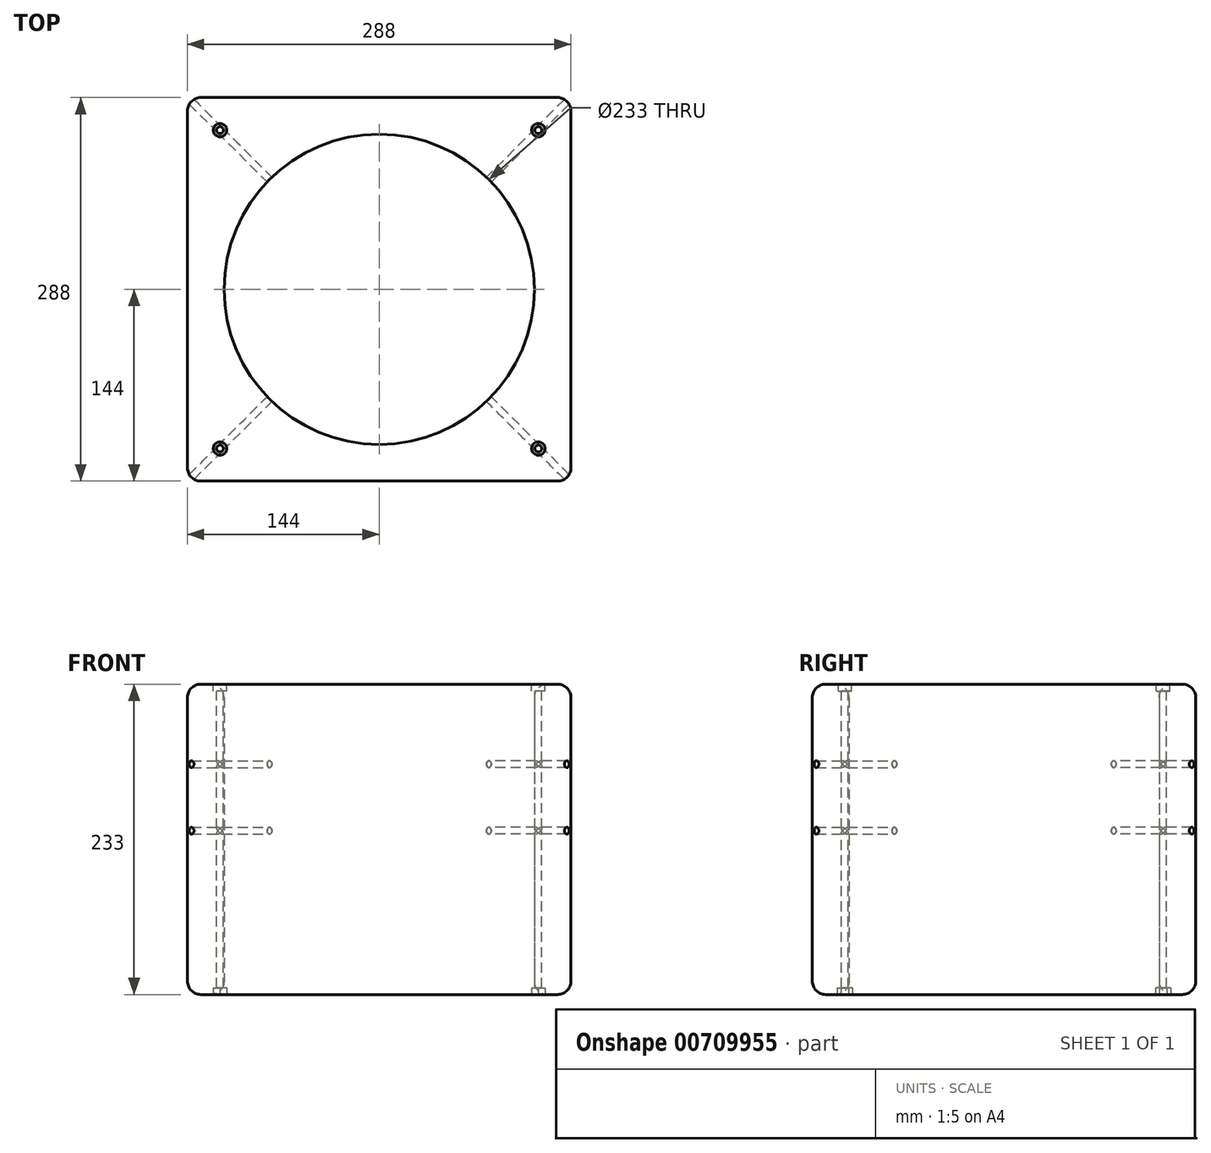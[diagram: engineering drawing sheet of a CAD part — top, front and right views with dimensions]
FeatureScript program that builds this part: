
annotation { "Feature Type Name" : "Feature", "Feature Type Description" : "" }
export const myFeature = defineFeature(function(context is Context, id is Id, definition is map)
    precondition{}
    {
        {
            var Q0;
            Q0=qCreatedBy(makeId("Top.planeOp"),FACE);
            var sketch = newSketch(context, id + "F0", { "sketchPlane" : qUnion([Q0])});
            skCircle(sketch, "E0", {"center": v(0, 0) * mm, "radius": 116.5 * mm});
            skLineSegment(sketch, "E1.bottom", {"start": v(144, 144) * mm, "end": v(-144, 144) * mm});
            skLineSegment(sketch, "E1.top", {"start": v(144, -144) * mm, "end": v(-144, -144) * mm});
            skLineSegment(sketch, "E1.left", {"start": v(144, 144) * mm, "end": v(144, -144) * mm});
            skLineSegment(sketch, "E1.right", {"start": v(-144, 144) * mm, "end": v(-144, -144) * mm});
            skSolve(sketch);
        }
        {
            var Q0;
            Q0=makeQuery(id+"F0.imprint","IMPRINT",FACE,{"disambiguationData":[TD([[makeQuery(id+"F0.imprint","IMPRINT",EDGE,{"derivedFrom":sQuery(id+"F0.wireOp",EDGE,"E0")}),-1.0]])]});
            extrude(context, id + "F1", {"entities" : qUnion([Q0]), "depth" : 233 * mm, "offsetDistance" : 25 * mm});
        }
        {
            var Q0;
            Q0=makeQuery(id+"F1.opExtrude","CAP_FACE",FACE,{"disambiguationData":[OSD([sQuery(id+"F0.wireOp",EDGE,"E0"),sQuery(id+"F0.wireOp",EDGE,"E1.bottom"),sQuery(id+"F0.wireOp",EDGE,"E1.top"),sQuery(id+"F0.wireOp",EDGE,"E1.left"),sQuery(id+"F0.wireOp",EDGE,"E1.right")])],"isStart":false});
            var Q1;
            Q1=makeQuery(id+"F1.opExtrude","CAP_FACE",FACE,{"disambiguationData":[OSD([sQuery(id+"F0.wireOp",EDGE,"E0"),sQuery(id+"F0.wireOp",EDGE,"E1.bottom"),sQuery(id+"F0.wireOp",EDGE,"E1.top"),sQuery(id+"F0.wireOp",EDGE,"E1.left"),sQuery(id+"F0.wireOp",EDGE,"E1.right")])],"isStart":true});
            var Q2;
            {var subQ0=sQuery(id+"F0.wireOp",EDGE,"E1.bottom");Q2=makeQuery(id+"Fkc3ZmtWVtNshut_1.opChamfer","BLEND_EDGE",EDGE,{"blendedFrom":[makeQuery(id+"F1.opExtrude","SWEPT_EDGE",EDGE,{"disambiguationData":[OSD([subQ0,sQuery(id+"F0.wireOp",EDGE,"E1.right")])]}),makeQuery(id+"F1.opExtrude","SWEPT_FACE",FACE,{"disambiguationData":[OSD([subQ0])]})],"blendedInto":[makeQuery(id+"F1.opExtrude","SWEPT_FACE",FACE,{"disambiguationData":[OSD([subQ0])]})]});}
            var Q3;
            Q3=makeQuery(id+"F1.opExtrude","SWEPT_FACE",FACE,{"disambiguationData":[OSD([sQuery(id+"F0.wireOp",EDGE,"E1.right")])]});
            var Q4;
            {var subQ0=sQuery(id+"F0.wireOp",EDGE,"E1.top");Q4=makeQuery(id+"Fkc3ZmtWVtNshut_1.opChamfer","BLEND_EDGE",EDGE,{"blendedFrom":[makeQuery(id+"F1.opExtrude","SWEPT_EDGE",EDGE,{"disambiguationData":[OSD([subQ0,sQuery(id+"F0.wireOp",EDGE,"E1.right")])]}),makeQuery(id+"F1.opExtrude","SWEPT_FACE",FACE,{"disambiguationData":[OSD([subQ0])]})],"blendedInto":[makeQuery(id+"F1.opExtrude","SWEPT_FACE",FACE,{"disambiguationData":[OSD([subQ0])]})]});}
            var Q5;
            {var subQ0=sQuery(id+"F0.wireOp",EDGE,"E1.top");Q5=makeQuery(id+"Fkc3ZmtWVtNshut_1.opChamfer","BLEND_EDGE",EDGE,{"blendedFrom":[makeQuery(id+"F1.opExtrude","SWEPT_EDGE",EDGE,{"disambiguationData":[OSD([subQ0,sQuery(id+"F0.wireOp",EDGE,"E1.left")])]}),makeQuery(id+"F1.opExtrude","SWEPT_FACE",FACE,{"disambiguationData":[OSD([subQ0])]})],"blendedInto":[makeQuery(id+"F1.opExtrude","SWEPT_FACE",FACE,{"disambiguationData":[OSD([subQ0])]})]});}
            var Q6;
            Q6=makeQuery(id+"Fkc3ZmtWVtNshut_1.opChamfer","BLEND_FACE",FACE,{"disambiguationData":[OSD([sQuery(id+"F0.wireOp",EDGE,"E1.top"),sQuery(id+"F0.wireOp",EDGE,"E1.left")])]});
            var Q7;
            Q7=makeQuery(id+"F1.opExtrude","SWEPT_FACE",FACE,{"disambiguationData":[OSD([sQuery(id+"F0.wireOp",EDGE,"E1.left")])]});
            var Q8;
            Q8=makeQuery(id+"Fkc3ZmtWVtNshut_1.opChamfer","BLEND_FACE",FACE,{"disambiguationData":[OSD([sQuery(id+"F0.wireOp",EDGE,"E1.bottom"),sQuery(id+"F0.wireOp",EDGE,"E1.left")])]});
            fillet(context, id + "F2", {"entities" : qUnion([Q0, Q1, Q2, Q3, Q4, Q5, Q6, Q7, Q8]), "radius" : 10 * mm, "tangentPropagation" : true, "allowEdgeOverflow" : false});
        }
        {
            var Q0;
            {var subQ0=sQuery(id+"F0.wireOp",EDGE,"E1.right");var subQ1=sQuery(id+"F0.wireOp",EDGE,"E1.top");Q0=makeQuery(id+"F2.opFillet","BLEND_VERTEX",VERTEX,{"blendedFrom":[makeQuery(id+"F1.opExtrude","CAP_VERTEX",VERTEX,{"disambiguationData":[OSD([subQ1,subQ0])],"isStart":false}),makeQuery(id+"F1.opExtrude","CAP_EDGE",EDGE,{"disambiguationData":[OSD([subQ1])],"isStart":false}),makeQuery(id+"F1.opExtrude","CAP_EDGE",EDGE,{"disambiguationData":[OSD([subQ0])],"isStart":false}),makeQuery(id+"F1.opExtrude","CAP_FACE",FACE,{"disambiguationData":[OSD([sQuery(id+"F0.wireOp",EDGE,"E0"),sQuery(id+"F0.wireOp",EDGE,"E1.bottom"),subQ1,sQuery(id+"F0.wireOp",EDGE,"E1.left"),subQ0])],"isStart":false})],"blendedInto":[makeQuery(id+"F1.opExtrude","CAP_FACE",FACE,{"disambiguationData":[OSD([sQuery(id+"F0.wireOp",EDGE,"E0"),sQuery(id+"F0.wireOp",EDGE,"E1.bottom"),subQ1,sQuery(id+"F0.wireOp",EDGE,"E1.left"),subQ0])],"isStart":false})]});}
            var Q1;
            {var subQ0=sQuery(id+"F0.wireOp",EDGE,"E1.left");var subQ1=sQuery(id+"F0.wireOp",EDGE,"E1.bottom");Q1=makeQuery(id+"F2.opFillet","BLEND_VERTEX",VERTEX,{"blendedFrom":[makeQuery(id+"F1.opExtrude","CAP_VERTEX",VERTEX,{"disambiguationData":[OSD([subQ1,subQ0])],"isStart":false}),makeQuery(id+"F1.opExtrude","CAP_EDGE",EDGE,{"disambiguationData":[OSD([subQ1])],"isStart":false}),makeQuery(id+"F1.opExtrude","CAP_EDGE",EDGE,{"disambiguationData":[OSD([subQ0])],"isStart":false}),makeQuery(id+"F1.opExtrude","CAP_FACE",FACE,{"disambiguationData":[OSD([sQuery(id+"F0.wireOp",EDGE,"E0"),subQ1,sQuery(id+"F0.wireOp",EDGE,"E1.top"),subQ0,sQuery(id+"F0.wireOp",EDGE,"E1.right")])],"isStart":false})],"blendedInto":[makeQuery(id+"F1.opExtrude","CAP_FACE",FACE,{"disambiguationData":[OSD([sQuery(id+"F0.wireOp",EDGE,"E0"),subQ1,sQuery(id+"F0.wireOp",EDGE,"E1.top"),subQ0,sQuery(id+"F0.wireOp",EDGE,"E1.right")])],"isStart":false})]});}
            var Q2;
            {var subQ0=sQuery(id+"F0.wireOp",EDGE,"E1.left");var subQ1=sQuery(id+"F0.wireOp",EDGE,"E1.bottom");Q2=makeQuery(id+"F2.opFillet","BLEND_VERTEX",VERTEX,{"blendedFrom":[makeQuery(id+"F1.opExtrude","CAP_VERTEX",VERTEX,{"disambiguationData":[OSD([subQ1,subQ0])],"isStart":true}),makeQuery(id+"F1.opExtrude","CAP_EDGE",EDGE,{"disambiguationData":[OSD([subQ1])],"isStart":true}),makeQuery(id+"F1.opExtrude","CAP_EDGE",EDGE,{"disambiguationData":[OSD([subQ0])],"isStart":true}),makeQuery(id+"F1.opExtrude","CAP_FACE",FACE,{"disambiguationData":[OSD([sQuery(id+"F0.wireOp",EDGE,"E0"),subQ1,sQuery(id+"F0.wireOp",EDGE,"E1.top"),subQ0,sQuery(id+"F0.wireOp",EDGE,"E1.right")])],"isStart":true})],"blendedInto":[makeQuery(id+"F1.opExtrude","CAP_FACE",FACE,{"disambiguationData":[OSD([sQuery(id+"F0.wireOp",EDGE,"E0"),subQ1,sQuery(id+"F0.wireOp",EDGE,"E1.top"),subQ0,sQuery(id+"F0.wireOp",EDGE,"E1.right")])],"isStart":true})]});}
            cPlane(context, id + "F3", {"entities" : qUnion([Q0, Q1, Q2]), "cplaneType" : CPlaneType.THREE_POINT, "offset" : 25 * mm, "width" : 150 * mm, "height" : 150 * mm});
        }
        {
            var Q0;
            {var subQ0=sQuery(id+"F0.wireOp",EDGE,"E1.left");var subQ1=sQuery(id+"F0.wireOp",EDGE,"E1.top");Q0=makeQuery(id+"F2.opFillet","BLEND_VERTEX",VERTEX,{"blendedFrom":[makeQuery(id+"F1.opExtrude","CAP_VERTEX",VERTEX,{"disambiguationData":[OSD([subQ1,subQ0])],"isStart":false}),makeQuery(id+"F1.opExtrude","CAP_EDGE",EDGE,{"disambiguationData":[OSD([subQ1])],"isStart":false}),makeQuery(id+"F1.opExtrude","CAP_EDGE",EDGE,{"disambiguationData":[OSD([subQ0])],"isStart":false}),makeQuery(id+"F1.opExtrude","CAP_FACE",FACE,{"disambiguationData":[OSD([sQuery(id+"F0.wireOp",EDGE,"E0"),sQuery(id+"F0.wireOp",EDGE,"E1.bottom"),subQ1,subQ0,sQuery(id+"F0.wireOp",EDGE,"E1.right")])],"isStart":false})],"blendedInto":[makeQuery(id+"F1.opExtrude","CAP_FACE",FACE,{"disambiguationData":[OSD([sQuery(id+"F0.wireOp",EDGE,"E0"),sQuery(id+"F0.wireOp",EDGE,"E1.bottom"),subQ1,subQ0,sQuery(id+"F0.wireOp",EDGE,"E1.right")])],"isStart":false})]});}
            var Q1;
            {var subQ0=sQuery(id+"F0.wireOp",EDGE,"E1.right");var subQ1=sQuery(id+"F0.wireOp",EDGE,"E1.bottom");Q1=makeQuery(id+"F2.opFillet","BLEND_VERTEX",VERTEX,{"blendedFrom":[makeQuery(id+"F1.opExtrude","CAP_VERTEX",VERTEX,{"disambiguationData":[OSD([subQ1,subQ0])],"isStart":false}),makeQuery(id+"F1.opExtrude","CAP_EDGE",EDGE,{"disambiguationData":[OSD([subQ1])],"isStart":false}),makeQuery(id+"F1.opExtrude","CAP_EDGE",EDGE,{"disambiguationData":[OSD([subQ0])],"isStart":false}),makeQuery(id+"F1.opExtrude","CAP_FACE",FACE,{"disambiguationData":[OSD([sQuery(id+"F0.wireOp",EDGE,"E0"),subQ1,sQuery(id+"F0.wireOp",EDGE,"E1.top"),sQuery(id+"F0.wireOp",EDGE,"E1.left"),subQ0])],"isStart":false})],"blendedInto":[makeQuery(id+"F1.opExtrude","CAP_FACE",FACE,{"disambiguationData":[OSD([sQuery(id+"F0.wireOp",EDGE,"E0"),subQ1,sQuery(id+"F0.wireOp",EDGE,"E1.top"),sQuery(id+"F0.wireOp",EDGE,"E1.left"),subQ0])],"isStart":false})]});}
            var Q2;
            {var subQ0=sQuery(id+"F0.wireOp",EDGE,"E1.right");var subQ1=sQuery(id+"F0.wireOp",EDGE,"E1.bottom");Q2=makeQuery(id+"F2.opFillet","BLEND_VERTEX",VERTEX,{"blendedFrom":[makeQuery(id+"F1.opExtrude","CAP_VERTEX",VERTEX,{"disambiguationData":[OSD([subQ1,subQ0])],"isStart":true}),makeQuery(id+"F1.opExtrude","CAP_EDGE",EDGE,{"disambiguationData":[OSD([subQ1])],"isStart":true}),makeQuery(id+"F1.opExtrude","CAP_EDGE",EDGE,{"disambiguationData":[OSD([subQ0])],"isStart":true}),makeQuery(id+"F1.opExtrude","CAP_FACE",FACE,{"disambiguationData":[OSD([sQuery(id+"F0.wireOp",EDGE,"E0"),subQ1,sQuery(id+"F0.wireOp",EDGE,"E1.top"),sQuery(id+"F0.wireOp",EDGE,"E1.left"),subQ0])],"isStart":true})],"blendedInto":[makeQuery(id+"F1.opExtrude","CAP_FACE",FACE,{"disambiguationData":[OSD([sQuery(id+"F0.wireOp",EDGE,"E0"),subQ1,sQuery(id+"F0.wireOp",EDGE,"E1.top"),sQuery(id+"F0.wireOp",EDGE,"E1.left"),subQ0])],"isStart":true})]});}
            cPlane(context, id + "F4", {"entities" : qUnion([Q0, Q1, Q2]), "cplaneType" : CPlaneType.THREE_POINT, "offset" : 25 * mm, "width" : 150 * mm, "height" : 150 * mm});
        }
        {
            var Q0;
            Q0=qCreatedBy(id+"F3.planeOp",FACE);
            var sketch = newSketch(context, id + "F5", { "sketchPlane" : qUnion([Q0])});
            skCircle(sketch, "E2", {"center": v(0, 173) * mm, "radius": 2.55 * mm});
            skCircle(sketch, "E3", {"center": v(0, 123) * mm, "radius": 2.55 * mm});
            skSolve(sketch);
        }
        {
            var Q0;
            Q0=qCreatedBy(id+"F4.planeOp",FACE);
            var sketch = newSketch(context, id + "F6", { "sketchPlane" : qUnion([Q0])});
            skCircle(sketch, "E4", {"center": v(0, 173) * mm, "radius": 2.55 * mm});
            skCircle(sketch, "E5", {"center": v(0, 123) * mm, "radius": 2.55 * mm});
            skSolve(sketch);
        }
        {
            var Q0;
            Q0=sQuery(id+"F5.wireOp",VERTEX,"E2.center");
            var Q1;
            Q1=sQuery(id+"F5.wireOp",VERTEX,"E3.center");
            var Q2;
            Q2=makeQuery(id+"F1.opExtrude","SWEPT_BODY",BODY,{"disambiguationData":[OSD([sQuery(id+"F0.wireOp",EDGE,"E0"),sQuery(id+"F0.wireOp",EDGE,"E1.bottom"),sQuery(id+"F0.wireOp",EDGE,"E1.top"),sQuery(id+"F0.wireOp",EDGE,"E1.left"),sQuery(id+"F0.wireOp",EDGE,"E1.right")])]});
            hole(context, id + "F7", {"style" : HoleStyle.SIMPLE, "endStyle" : HoleEndStyle.THROUGH, "holeDiameter" : 5.1 * mm, "majorDiameter" : 5 * mm, "isTappedThrough" : true, "tappedDepth" : 12 * mm, "tapClearance" : 3, "locations" : qUnion([Q0, Q1]), "scope" : qUnion([Q2])});
        }
        {
            var Q0;
            Q0=sQuery(id+"F5.wireOp",VERTEX,"E2.center");
            var Q1;
            Q1=sQuery(id+"F5.wireOp",VERTEX,"E3.center");
            var Q2;
            Q2=makeQuery(id+"F1.opExtrude","SWEPT_BODY",BODY,{"disambiguationData":[OSD([sQuery(id+"F0.wireOp",EDGE,"E0"),sQuery(id+"F0.wireOp",EDGE,"E1.bottom"),sQuery(id+"F0.wireOp",EDGE,"E1.top"),sQuery(id+"F0.wireOp",EDGE,"E1.left"),sQuery(id+"F0.wireOp",EDGE,"E1.right")])]});
            hole(context, id + "F8", {"style" : HoleStyle.SIMPLE, "endStyle" : HoleEndStyle.THROUGH, "oppositeDirection" : true, "holeDiameter" : 5.1 * mm, "majorDiameter" : 5 * mm, "isTappedThrough" : true, "tappedDepth" : 12 * mm, "tapClearance" : 3, "locations" : qUnion([Q0, Q1]), "scope" : qUnion([Q2])});
        }
        {
            var Q0;
            Q0=sQuery(id+"F6.wireOp",VERTEX,"E4.center");
            var Q1;
            Q1=sQuery(id+"F6.wireOp",VERTEX,"E5.center");
            var Q2;
            Q2=makeQuery(id+"F1.opExtrude","SWEPT_BODY",BODY,{"disambiguationData":[OSD([sQuery(id+"F0.wireOp",EDGE,"E0"),sQuery(id+"F0.wireOp",EDGE,"E1.bottom"),sQuery(id+"F0.wireOp",EDGE,"E1.top"),sQuery(id+"F0.wireOp",EDGE,"E1.left"),sQuery(id+"F0.wireOp",EDGE,"E1.right")])]});
            hole(context, id + "F9", {"style" : HoleStyle.SIMPLE, "endStyle" : HoleEndStyle.THROUGH, "holeDiameter" : 5.1 * mm, "majorDiameter" : 5 * mm, "isTappedThrough" : true, "tappedDepth" : 12 * mm, "tapClearance" : 3, "locations" : qUnion([Q0, Q1]), "scope" : qUnion([Q2])});
        }
        {
            var Q0;
            Q0=sQuery(id+"F6.wireOp",VERTEX,"E4.center");
            var Q1;
            Q1=sQuery(id+"F6.wireOp",VERTEX,"E5.center");
            var Q2;
            Q2=makeQuery(id+"F1.opExtrude","SWEPT_BODY",BODY,{"disambiguationData":[OSD([sQuery(id+"F0.wireOp",EDGE,"E0"),sQuery(id+"F0.wireOp",EDGE,"E1.bottom"),sQuery(id+"F0.wireOp",EDGE,"E1.top"),sQuery(id+"F0.wireOp",EDGE,"E1.left"),sQuery(id+"F0.wireOp",EDGE,"E1.right")])]});
            hole(context, id + "F10", {"style" : HoleStyle.SIMPLE, "endStyle" : HoleEndStyle.THROUGH, "oppositeDirection" : true, "holeDiameter" : 5.1 * mm, "majorDiameter" : 5 * mm, "isTappedThrough" : true, "tappedDepth" : 12 * mm, "tapClearance" : 3, "locations" : qUnion([Q0, Q1]), "scope" : qUnion([Q2])});
        }
        {
            var Q0;
            Q0=makeQuery(id+"F1.opExtrude","CAP_FACE",FACE,{"disambiguationData":[OSD([sQuery(id+"F0.wireOp",EDGE,"E0"),sQuery(id+"F0.wireOp",EDGE,"E1.bottom"),sQuery(id+"F0.wireOp",EDGE,"E1.top"),sQuery(id+"F0.wireOp",EDGE,"E1.left"),sQuery(id+"F0.wireOp",EDGE,"E1.right")])],"isStart":false});
            var sketch = newSketch(context, id + "F11", { "sketchPlane" : qUnion([Q0])});
            skLineSegment(sketch, "E6.bottom", {"start": v(119.54, 119.54) * mm, "end": v(-119.54, 119.54) * mm});
            skLineSegment(sketch, "E6.top", {"start": v(119.54, -119.54) * mm, "end": v(-119.54, -119.54) * mm});
            skLineSegment(sketch, "E6.left", {"start": v(119.54, 119.54) * mm, "end": v(119.54, -119.54) * mm});
            skLineSegment(sketch, "E6.right", {"start": v(-119.54, 119.54) * mm, "end": v(-119.54, -119.54) * mm});
            skPoint(sketch, "E6.middle", {"position": v(0, 0) * mm});
            skCircle(sketch, "E7", {"center": v(-119.54, -119.54) * mm, "radius": 2.55 * mm});
            skCircle(sketch, "E8", {"center": v(119.54, -119.54) * mm, "radius": 2.55 * mm});
            skCircle(sketch, "E9", {"center": v(119.54, 119.54) * mm, "radius": 2.55 * mm});
            skCircle(sketch, "E10", {"center": v(-119.54, 119.54) * mm, "radius": 2.55 * mm});
            skSolve(sketch);
        }
        {
            var Q0;
            Q0=sQuery(id+"F11.wireOp",VERTEX,"E7.center");
            var Q1;
            Q1=sQuery(id+"F11.wireOp",VERTEX,"E8.center");
            var Q2;
            Q2=sQuery(id+"F11.wireOp",VERTEX,"E9.center");
            var Q3;
            Q3=sQuery(id+"F11.wireOp",VERTEX,"E10.center");
            var Q4;
            Q4=makeQuery(id+"F1.opExtrude","SWEPT_BODY",BODY,{"disambiguationData":[OSD([sQuery(id+"F0.wireOp",EDGE,"E0"),sQuery(id+"F0.wireOp",EDGE,"E1.bottom"),sQuery(id+"F0.wireOp",EDGE,"E1.top"),sQuery(id+"F0.wireOp",EDGE,"E1.left"),sQuery(id+"F0.wireOp",EDGE,"E1.right")])]});
            hole(context, id + "F12", {"style" : HoleStyle.C_BORE, "endStyle" : HoleEndStyle.THROUGH, "holeDiameter" : 5.1 * mm, "cBoreDiameter" : 10 * mm, "cBoreDepth" : 5 * mm, "majorDiameter" : 5 * mm, "isTappedThrough" : true, "tappedDepth" : 12 * mm, "tapClearance" : 3, "locations" : qUnion([Q0, Q1, Q2, Q3]), "scope" : qUnion([Q4])});
        }
        {
            var Q0;
            Q0=makeQuery(id+"F0.imprint","IMPRINT",FACE,{"disambiguationData":[TD([[makeQuery(id+"F0.imprint","IMPRINT",EDGE,{"derivedFrom":sQuery(id+"F0.wireOp",EDGE,"E0")}),-1.0]])]});
            var sketch = newSketch(context, id + "F13", { "sketchPlane" : qUnion([Q0])});
            skLineSegment(sketch, "E11.bottom", {"start": v(119.54, -119.54) * mm, "end": v(-119.54, -119.54) * mm});
            skLineSegment(sketch, "E11.top", {"start": v(119.54, 119.54) * mm, "end": v(-119.54, 119.54) * mm});
            skLineSegment(sketch, "E11.left", {"start": v(119.54, -119.54) * mm, "end": v(119.54, 119.54) * mm});
            skLineSegment(sketch, "E11.right", {"start": v(-119.54, -119.54) * mm, "end": v(-119.54, 119.54) * mm});
            skPoint(sketch, "E11.middle", {"position": v(0, 0) * mm});
            skCircle(sketch, "E12.cCircle", {"center": v(-119.54, 119.54) * mm, "radius": 5 * mm, "construction": true});
            skLineSegment(sketch, "E12.0", {"start": v(-114.54, 122.42) * mm, "end": v(-114.54, 116.65) * mm});
            skLineSegment(sketch, "E12.1", {"start": v(-114.54, 116.65) * mm, "end": v(-119.54, 113.76) * mm});
            skLineSegment(sketch, "E12.2", {"start": v(-119.54, 113.76) * mm, "end": v(-124.54, 116.65) * mm});
            skLineSegment(sketch, "E12.3", {"start": v(-124.54, 116.65) * mm, "end": v(-124.54, 122.42) * mm});
            skLineSegment(sketch, "E12.4", {"start": v(-124.54, 122.42) * mm, "end": v(-119.54, 125.3) * mm});
            skLineSegment(sketch, "E12.5", {"start": v(-119.54, 125.3) * mm, "end": v(-114.54, 122.42) * mm});
            skPoint(sketch, "E12.0.midPoint", {"position": v(-114.54, 119.54) * mm});
            skCircle(sketch, "E13.cCircle", {"center": v(119.54, 119.54) * mm, "radius": 5 * mm, "construction": true});
            skLineSegment(sketch, "E13.0", {"start": v(114.54, 116.65) * mm, "end": v(114.54, 122.42) * mm});
            skLineSegment(sketch, "E13.1", {"start": v(114.54, 122.42) * mm, "end": v(119.54, 125.3) * mm});
            skLineSegment(sketch, "E13.2", {"start": v(119.54, 125.3) * mm, "end": v(124.54, 122.42) * mm});
            skLineSegment(sketch, "E13.3", {"start": v(124.54, 122.42) * mm, "end": v(124.54, 116.65) * mm});
            skLineSegment(sketch, "E13.4", {"start": v(124.54, 116.65) * mm, "end": v(119.54, 113.76) * mm});
            skLineSegment(sketch, "E13.5", {"start": v(119.54, 113.76) * mm, "end": v(114.54, 116.65) * mm});
            skPoint(sketch, "E13.0.midPoint", {"position": v(114.54, 119.54) * mm});
            skCircle(sketch, "E14.cCircle", {"center": v(119.54, -119.54) * mm, "radius": 5 * mm, "construction": true});
            skLineSegment(sketch, "E14.0", {"start": v(114.54, -122.42) * mm, "end": v(114.54, -116.65) * mm});
            skLineSegment(sketch, "E14.1", {"start": v(114.54, -116.65) * mm, "end": v(119.54, -113.76) * mm});
            skLineSegment(sketch, "E14.2", {"start": v(119.54, -113.76) * mm, "end": v(124.54, -116.65) * mm});
            skLineSegment(sketch, "E14.3", {"start": v(124.54, -116.65) * mm, "end": v(124.54, -122.42) * mm});
            skLineSegment(sketch, "E14.4", {"start": v(124.54, -122.42) * mm, "end": v(119.54, -125.3) * mm});
            skLineSegment(sketch, "E14.5", {"start": v(119.54, -125.3) * mm, "end": v(114.54, -122.42) * mm});
            skPoint(sketch, "E14.0.midPoint", {"position": v(114.54, -119.54) * mm});
            skCircle(sketch, "E15.cCircle", {"center": v(-119.54, -119.54) * mm, "radius": 5 * mm, "construction": true});
            skLineSegment(sketch, "E15.0", {"start": v(-114.54, -116.65) * mm, "end": v(-114.54, -122.42) * mm});
            skLineSegment(sketch, "E15.1", {"start": v(-114.54, -122.42) * mm, "end": v(-119.54, -125.3) * mm});
            skLineSegment(sketch, "E15.2", {"start": v(-119.54, -125.3) * mm, "end": v(-124.54, -122.42) * mm});
            skLineSegment(sketch, "E15.3", {"start": v(-124.54, -122.42) * mm, "end": v(-124.54, -116.65) * mm});
            skLineSegment(sketch, "E15.4", {"start": v(-124.54, -116.65) * mm, "end": v(-119.54, -113.76) * mm});
            skLineSegment(sketch, "E15.5", {"start": v(-119.54, -113.76) * mm, "end": v(-114.54, -116.65) * mm});
            skPoint(sketch, "E15.0.midPoint", {"position": v(-114.54, -119.54) * mm});
            skSolve(sketch);
        }
        {
            var Q0;
            {var subQ6=sQuery(id+"F13.wireOp",EDGE,"E12.2");Q0=makeQuery(id+"F13.imprint","IMPRINT",FACE,{"disambiguationData":[TD([[makeQuery(id+"F13.imprint","IMPRINT",EDGE,{"derivedFrom":subQ6}),-1.0]])]});}
            var Q1;
            {var subQ5=sQuery(id+"F13.wireOp",EDGE,"E12.1");Q1=makeQuery(id+"F13.imprint","IMPRINT",FACE,{"disambiguationData":[TD([[makeQuery(id+"F13.imprint","IMPRINT",EDGE,{"derivedFrom":subQ5}),-1.0]])]});}
            var Q2;
            {var subQ5=sQuery(id+"F13.wireOp",EDGE,"E13.5");Q2=makeQuery(id+"F13.imprint","IMPRINT",FACE,{"disambiguationData":[TD([[makeQuery(id+"F13.imprint","IMPRINT",EDGE,{"derivedFrom":subQ5}),-1.0]])]});}
            var Q3;
            {var subQ0=sQuery(id+"F13.wireOp",EDGE,"E13.1");Q3=makeQuery(id+"F13.imprint","IMPRINT",FACE,{"disambiguationData":[TD([[makeQuery(id+"F13.imprint","IMPRINT",EDGE,{"derivedFrom":subQ0}),-1.0]])]});}
            var Q4;
            {var subQ5=sQuery(id+"F13.wireOp",EDGE,"E14.1");Q4=makeQuery(id+"F13.imprint","IMPRINT",FACE,{"disambiguationData":[TD([[makeQuery(id+"F13.imprint","IMPRINT",EDGE,{"derivedFrom":subQ5}),-1.0]])]});}
            var Q5;
            {var subQ0=sQuery(id+"F13.wireOp",EDGE,"E14.2");Q5=makeQuery(id+"F13.imprint","IMPRINT",FACE,{"disambiguationData":[TD([[makeQuery(id+"F13.imprint","IMPRINT",EDGE,{"derivedFrom":subQ0}),-1.0]])]});}
            var Q6;
            {var subQ5=sQuery(id+"F13.wireOp",EDGE,"E15.5");Q6=makeQuery(id+"F13.imprint","IMPRINT",FACE,{"disambiguationData":[TD([[makeQuery(id+"F13.imprint","IMPRINT",EDGE,{"derivedFrom":subQ5}),-1.0]])]});}
            var Q7;
            {var subQ0=sQuery(id+"F13.wireOp",EDGE,"E15.1");Q7=makeQuery(id+"F13.imprint","IMPRINT",FACE,{"disambiguationData":[TD([[makeQuery(id+"F13.imprint","IMPRINT",EDGE,{"derivedFrom":subQ0}),-1.0]])]});}
            extrude(context, id + "F14", {"entities" : qUnion([Q0, Q1, Q2, Q3, Q4, Q5, Q6, Q7]), "operationType" : NewBodyOperationType.REMOVE, "depth" : 5 * mm, "offsetDistance" : 25 * mm});
        }
    });
